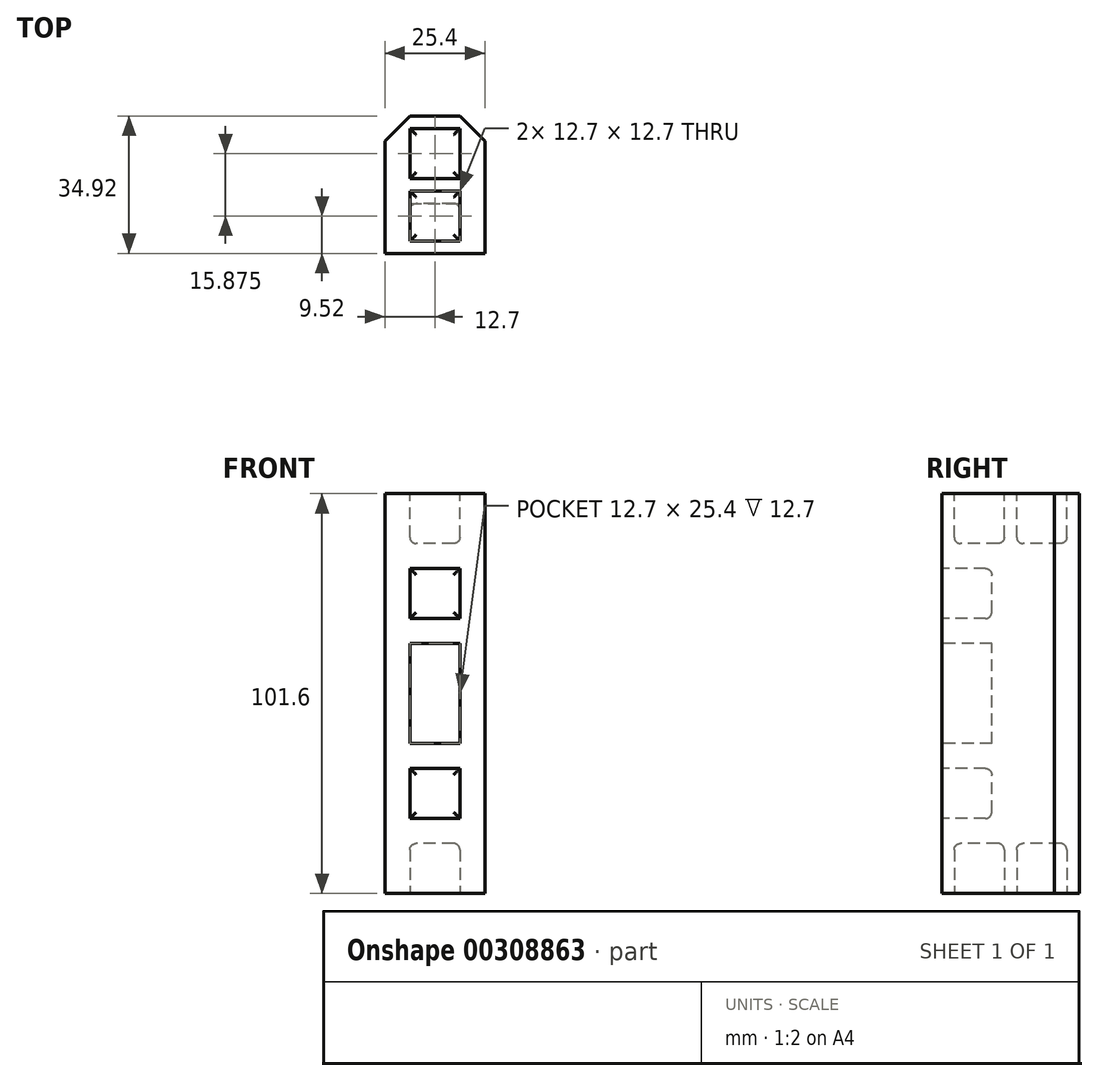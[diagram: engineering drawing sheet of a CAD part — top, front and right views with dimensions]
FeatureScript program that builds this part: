
annotation { "Feature Type Name" : "Feature", "Feature Type Description" : "" }
export const myFeature = defineFeature(function(context is Context, id is Id, definition is map)
    precondition{}
    {
        {
            var Q0;
            Q0=qCreatedBy(makeId("Front.planeOp"),FACE);
            var sketch = newSketch(context, id + "F0", { "sketchPlane" : qUnion([Q0])});
            skLineSegment(sketch, "E0.bottom", {"start": v(-12.7, -50.8) * mm, "end": v(12.7, -50.8) * mm});
            skLineSegment(sketch, "E0.top", {"start": v(-12.7, 50.8) * mm, "end": v(12.7, 50.8) * mm});
            skLineSegment(sketch, "E0.left", {"start": v(-12.7, -50.8) * mm, "end": v(-12.7, 50.8) * mm});
            skLineSegment(sketch, "E0.right", {"start": v(12.7, -50.8) * mm, "end": v(12.7, 50.8) * mm});
            skPoint(sketch, "E0.middle", {"position": v(0, 0) * mm});
            skSolve(sketch);
        }
        {
            var Q0;
            Q0 = qSketchRegion(id + "F0", true);
            extrude(context, id + "F1", {"entities" : qUnion([Q0]), "depth" : 34.92 * mm});
        }
        {
            var Q0;
            Q0=makeQuery(id+"F1.opExtrude","SWEPT_FACE",FACE,{"disambiguationData":[OSD([sQuery(id+"F0.wireOp",EDGE,"E0.top")])]});
            var sketch = newSketch(context, id + "F2", { "sketchPlane" : qUnion([Q0])});
            skLineSegment(sketch, "E1.bottom", {"start": v(6.35, -3.17) * mm, "end": v(-6.35, -3.17) * mm});
            skLineSegment(sketch, "E1.top", {"start": v(6.35, -15.88) * mm, "end": v(-6.35, -15.88) * mm});
            skLineSegment(sketch, "E1.left", {"start": v(6.35, -3.17) * mm, "end": v(6.35, -15.88) * mm});
            skLineSegment(sketch, "E1.right", {"start": v(-6.35, -3.17) * mm, "end": v(-6.35, -15.88) * mm});
            skPoint(sketch, "E1.middle", {"position": v(0, -9.52) * mm});
            skLineSegment(sketch, "E2.bottom", {"start": v(6.35, -19.05) * mm, "end": v(-6.35, -19.05) * mm});
            skLineSegment(sketch, "E2.top", {"start": v(6.35, -31.75) * mm, "end": v(-6.35, -31.75) * mm});
            skLineSegment(sketch, "E2.left", {"start": v(6.35, -19.05) * mm, "end": v(6.35, -31.75) * mm});
            skLineSegment(sketch, "E2.right", {"start": v(-6.35, -19.05) * mm, "end": v(-6.35, -31.75) * mm});
            skPoint(sketch, "E2.middle", {"position": v(0, -25.4) * mm});
            skSolve(sketch);
        }
        {
            var Q0;
            Q0 = qSketchRegion(id + "F2", true);
            extrude(context, id + "F3", {"entities" : qUnion([Q0]), "operationType" : NewBodyOperationType.REMOVE, "oppositeDirection" : true, "depth" : 12.7 * mm});
        }
        {
            var Q0;
            Q0=makeQuery(id+"F3.boolean.opBoolean","COPY",FACE,{"derivedFrom":makeQuery(id+"F3.opExtrude","CAP_FACE",FACE,{"disambiguationData":[OSD([sQuery(id+"F2.wireOp",EDGE,"E1.bottom"),sQuery(id+"F2.wireOp",EDGE,"E1.top"),sQuery(id+"F2.wireOp",EDGE,"E1.left"),sQuery(id+"F2.wireOp",EDGE,"E1.right")])],"isStart":false})});
            var Q1;
            Q1=makeQuery(id+"F3.boolean.opBoolean","COPY",FACE,{"derivedFrom":makeQuery(id+"F3.opExtrude","CAP_FACE",FACE,{"disambiguationData":[OSD([sQuery(id+"F2.wireOp",EDGE,"E2.bottom"),sQuery(id+"F2.wireOp",EDGE,"E2.top"),sQuery(id+"F2.wireOp",EDGE,"E2.left"),sQuery(id+"F2.wireOp",EDGE,"E2.right")])],"isStart":false})});
            fillet(context, id + "F4", {"entities" : qUnion([Q0, Q1]), "radius" : 1.59 * mm, "tangentPropagation" : true, "allowEdgeOverflow" : false});
        }
        {
            var Q0;
            Q0=makeQuery(id+"F1.opExtrude","SWEPT_FACE",FACE,{"disambiguationData":[OSD([sQuery(id+"F0.wireOp",EDGE,"E0.bottom")])]});
            var sketch = newSketch(context, id + "F5", { "sketchPlane" : qUnion([Q0])});
            skLineSegment(sketch, "E3.bottom", {"start": v(6.35, 3.18) * mm, "end": v(-6.35, 3.18) * mm});
            skLineSegment(sketch, "E3.top", {"start": v(6.35, 15.88) * mm, "end": v(-6.35, 15.88) * mm});
            skLineSegment(sketch, "E3.left", {"start": v(6.35, 3.18) * mm, "end": v(6.35, 15.88) * mm});
            skLineSegment(sketch, "E3.right", {"start": v(-6.35, 3.18) * mm, "end": v(-6.35, 15.88) * mm});
            skPoint(sketch, "E3.middle", {"position": v(0, 9.53) * mm});
            skLineSegment(sketch, "E4.bottom", {"start": v(6.35, 19.05) * mm, "end": v(-6.35, 19.05) * mm});
            skLineSegment(sketch, "E4.top", {"start": v(6.35, 31.75) * mm, "end": v(-6.35, 31.75) * mm});
            skLineSegment(sketch, "E4.left", {"start": v(6.35, 19.05) * mm, "end": v(6.35, 31.75) * mm});
            skLineSegment(sketch, "E4.right", {"start": v(-6.35, 19.05) * mm, "end": v(-6.35, 31.75) * mm});
            skPoint(sketch, "E4.middle", {"position": v(0, 25.4) * mm});
            skSolve(sketch);
        }
        {
            var Q0;
            Q0 = qSketchRegion(id + "F5", true);
            extrude(context, id + "F6", {"entities" : qUnion([Q0]), "operationType" : NewBodyOperationType.REMOVE, "oppositeDirection" : true, "depth" : 12.7 * mm});
        }
        {
            var Q0;
            Q0=makeQuery(id+"F6.boolean.opBoolean","COPY",FACE,{"derivedFrom":makeQuery(id+"F6.opExtrude","CAP_FACE",FACE,{"disambiguationData":[OSD([sQuery(id+"F5.wireOp",EDGE,"E3.bottom"),sQuery(id+"F5.wireOp",EDGE,"E3.top"),sQuery(id+"F5.wireOp",EDGE,"E3.left"),sQuery(id+"F5.wireOp",EDGE,"E3.right")])],"isStart":false})});
            var Q1;
            Q1=makeQuery(id+"F6.boolean.opBoolean","COPY",FACE,{"derivedFrom":makeQuery(id+"F6.opExtrude","CAP_FACE",FACE,{"disambiguationData":[OSD([sQuery(id+"F5.wireOp",EDGE,"E4.bottom"),sQuery(id+"F5.wireOp",EDGE,"E4.top"),sQuery(id+"F5.wireOp",EDGE,"E4.left"),sQuery(id+"F5.wireOp",EDGE,"E4.right")])],"isStart":false})});
            fillet(context, id + "F7", {"entities" : qUnion([Q0, Q1]), "radius" : 1.59 * mm, "tangentPropagation" : true, "allowEdgeOverflow" : false});
        }
        {
            var Q0;
            Q0=makeQuery(id+"F1.opExtrude","CAP_FACE",FACE,{"disambiguationData":[OSD([sQuery(id+"F0.wireOp",EDGE,"E0.bottom"),sQuery(id+"F0.wireOp",EDGE,"E0.top"),sQuery(id+"F0.wireOp",EDGE,"E0.left"),sQuery(id+"F0.wireOp",EDGE,"E0.right")])],"isStart":false});
            var sketch = newSketch(context, id + "F8", { "sketchPlane" : qUnion([Q0])});
            skLineSegment(sketch, "E5.bottom", {"start": v(6.35, 19.05) * mm, "end": v(-6.35, 19.05) * mm});
            skLineSegment(sketch, "E5.top", {"start": v(6.35, 31.75) * mm, "end": v(-6.35, 31.75) * mm});
            skLineSegment(sketch, "E5.left", {"start": v(6.35, 19.05) * mm, "end": v(6.35, 31.75) * mm});
            skLineSegment(sketch, "E5.right", {"start": v(-6.35, 19.05) * mm, "end": v(-6.35, 31.75) * mm});
            skPoint(sketch, "E5.middle", {"position": v(0, 25.4) * mm});
            skLineSegment(sketch, "E6.bottom", {"start": v(6.35, -31.75) * mm, "end": v(-6.35, -31.75) * mm});
            skLineSegment(sketch, "E6.top", {"start": v(6.35, -19.05) * mm, "end": v(-6.35, -19.05) * mm});
            skLineSegment(sketch, "E6.left", {"start": v(6.35, -31.75) * mm, "end": v(6.35, -19.05) * mm});
            skLineSegment(sketch, "E6.right", {"start": v(-6.35, -31.75) * mm, "end": v(-6.35, -19.05) * mm});
            skPoint(sketch, "E6.middle", {"position": v(0, -25.4) * mm});
            skSolve(sketch);
        }
        {
            var Q0;
            Q0 = qSketchRegion(id + "F8", true);
            extrude(context, id + "F9", {"entities" : qUnion([Q0]), "operationType" : NewBodyOperationType.REMOVE, "oppositeDirection" : true, "depth" : 12.7 * mm});
        }
        {
            var Q0;
            Q0=makeQuery(id+"F9.boolean.opBoolean","COPY",FACE,{"derivedFrom":makeQuery(id+"F9.opExtrude","CAP_FACE",FACE,{"disambiguationData":[OSD([sQuery(id+"F8.wireOp",EDGE,"E5.bottom"),sQuery(id+"F8.wireOp",EDGE,"E5.top"),sQuery(id+"F8.wireOp",EDGE,"E5.left"),sQuery(id+"F8.wireOp",EDGE,"E5.right")])],"isStart":false})});
            var Q1;
            Q1=makeQuery(id+"F9.boolean.opBoolean","COPY",FACE,{"derivedFrom":makeQuery(id+"F9.opExtrude","CAP_FACE",FACE,{"disambiguationData":[OSD([sQuery(id+"F8.wireOp",EDGE,"E6.bottom"),sQuery(id+"F8.wireOp",EDGE,"E6.top"),sQuery(id+"F8.wireOp",EDGE,"E6.left"),sQuery(id+"F8.wireOp",EDGE,"E6.right")])],"isStart":false})});
            fillet(context, id + "F10", {"entities" : qUnion([Q0, Q1]), "radius" : 1.59 * mm, "tangentPropagation" : true, "allowEdgeOverflow" : false});
        }
        {
            var Q0;
            Q0=makeQuery(id+"F1.opExtrude","CAP_EDGE",EDGE,{"disambiguationData":[OSD([sQuery(id+"F0.wireOp",EDGE,"E0.right")])],"isStart":true});
            var Q1;
            Q1=makeQuery(id+"F1.opExtrude","CAP_EDGE",EDGE,{"disambiguationData":[OSD([sQuery(id+"F0.wireOp",EDGE,"E0.left")])],"isStart":true});
            chamfer(context, id + "F11", {"entities" : qUnion([Q0, Q1]), "width" : 6.35 * mm, "tangentPropagation" : true});
        }
        {
            var Q0;
            Q0=makeQuery(id+"F1.opExtrude","CAP_FACE",FACE,{"disambiguationData":[OSD([sQuery(id+"F0.wireOp",EDGE,"E0.bottom"),sQuery(id+"F0.wireOp",EDGE,"E0.top"),sQuery(id+"F0.wireOp",EDGE,"E0.left"),sQuery(id+"F0.wireOp",EDGE,"E0.right")])],"isStart":false});
            var sketch = newSketch(context, id + "F12", { "sketchPlane" : qUnion([Q0])});
            skLineSegment(sketch, "E7.bottom", {"start": v(-6.35, -12.7) * mm, "end": v(6.35, -12.7) * mm});
            skLineSegment(sketch, "E7.top", {"start": v(-6.35, 12.7) * mm, "end": v(6.35, 12.7) * mm});
            skLineSegment(sketch, "E7.left", {"start": v(-6.35, -12.7) * mm, "end": v(-6.35, 12.7) * mm});
            skLineSegment(sketch, "E7.right", {"start": v(6.35, -12.7) * mm, "end": v(6.35, 12.7) * mm});
            skPoint(sketch, "E7.middle", {"position": v(0, 0) * mm});
            skSolve(sketch);
        }
        {
            var Q0;
            Q0 = qSketchRegion(id + "F12", true);
            extrude(context, id + "F13", {"entities" : qUnion([Q0]), "operationType" : NewBodyOperationType.REMOVE, "oppositeDirection" : true, "depth" : 12.7 * mm});
        }
    });
